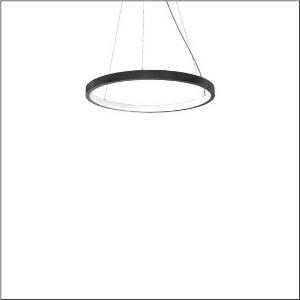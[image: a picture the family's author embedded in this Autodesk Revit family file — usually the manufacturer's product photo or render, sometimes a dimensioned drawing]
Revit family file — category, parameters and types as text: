
# Revit family: silica_21_ring-i_5pjbi2d1104a
name_source: partatom
category: Lighting Fixtures
units: mm (PartAtom-declared; Revit-internal decimal feet)

## family parameters
Cut with Voids When Loaded = No
Host = Face
Light Source = No
Part Type = Normal
Room Calculation Point = No
Round Connector Dimension = Use Diameter
Shared = No

## types (1)
- Silica 21 Ring-I (1 x LED, 4800 lm, 80 W, 3000K)
    Apparent Load = 80 VA
    CIE Flux Codes = 22 48 76 50 101
    Color Rendering = 80
    Color Temperature = 3000K
    Default Elevation = 1800 mm
    Description = Silica 21 Ring-I, suspended luminaire, of PMMA, frosted, light emission: inner ring side luminous distribution, primary light characteristic: symmetric, installation type: suspended mounting, LED, rated luminous flux: 4.800lm, luminous efficacy: 60lm/W, light colour: 830, colour temperature: 3000K, control gear: DALI 2, with terminal, 5-pole, mains connection: 230V, AC/DC, 0/50..60Hz, rated input power: 80W, housing, of extruded aluminium section, jet black (RAL 9005), diameter: 805mm, ceiling canopy, jet black (RAL 9005), protection rating (lamp compartment): IP40, insulation class (complete): insulation class I (protective earthing), certification: CE, impact resistance: IK02, permissible operating ambient temperature: 0..+35°C, packaging unit: 1 piece
    Height = 48 mm  [stored 0.15748 ft]
    Lamp = 1 x LED
    Lamp Light Flux = 4800 lm
    Lamp Power = 80 W
    Lamp count = 1
    Length = 805 mm
    Luminous efficacy = 60 lm/W
    Manufacturer = Siteco
    ModVariant = No
    Model = 5PJBI2D1104A
    Mounting Place = Ceiling
    Mounting Type = Pendant
    Number of Poles = 1
    OnlyDefault = Yes
    Power Factor = 1
    Product Name = Silica 21 Ring-I
    Product group = suspended luminaire
    ProductGroupID = 904
    Protection Class = Protection class I
    Protection Degree = IP 40
    RLX_Detail_Level = 1
    RLX_Emergency_Light_Flux = 0 lm
    RLX_Emergency_Type = 0
    RLX_Emergency_Type_DB = No
    RlxData = <blob elided: 13917 chars, md5=37fd4ea5>
    Socket = socket
    Standby Power = 0 W
    System Light Flux = 4800 lm
    System Power = 80 W
    Type Comments = Product without accessories
    Type Image = l_1258365.jpg
    URL = http://relux.com
    VarID = ---
    Voltage = 0 V
    Weight = 0.00 kg
    Width = 0 mm  [stored 0 ft]

note: [stored X ft] marks values corroborated as IEEE doubles in the binary element streams (Revit-internal decimal feet)

## geometry (parser evidence)
native form markers: Sweep x13
no freeform markers — native parametric forms only
